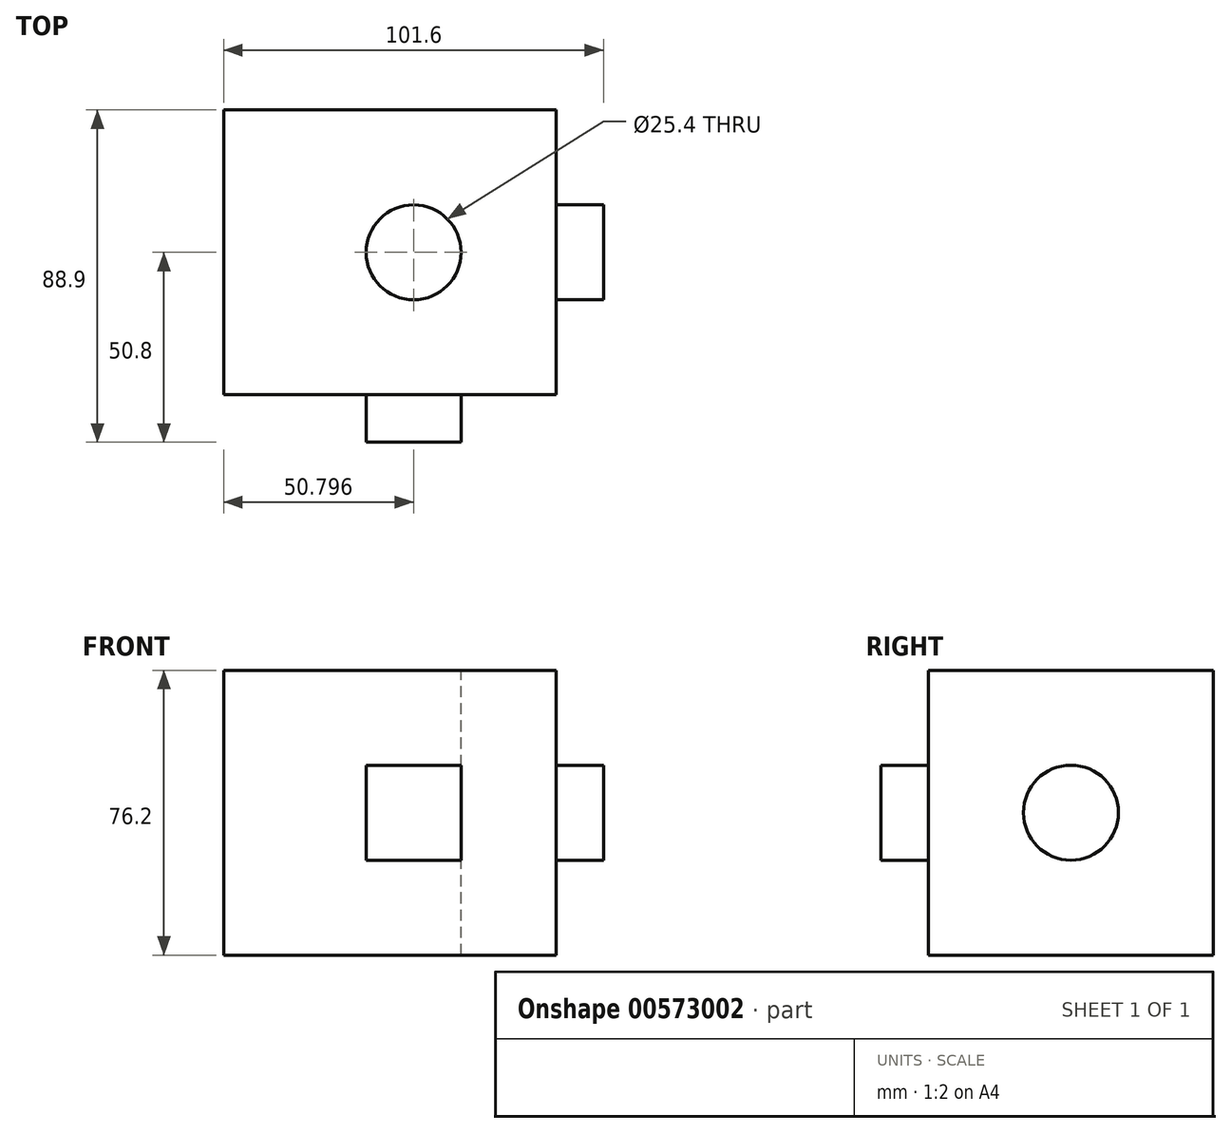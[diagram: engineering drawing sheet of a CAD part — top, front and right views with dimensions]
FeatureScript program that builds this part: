
annotation { "Feature Type Name" : "Feature", "Feature Type Description" : "" }
export const myFeature = defineFeature(function(context is Context, id is Id, definition is map)
    precondition{}
    {
        {
            var Q0;
            Q0=qCreatedBy(makeId("Front.planeOp"),FACE);
            var sketch = newSketch(context, id + "F0", { "sketchPlane" : qUnion([Q0])});
            skLineSegment(sketch, "E0.bottom", {"start": v(-75.57, 74.05) * mm, "end": v(0.63, 74.05) * mm});
            skLineSegment(sketch, "E0.top", {"start": v(-75.57, -2.15) * mm, "end": v(0.63, -2.15) * mm});
            skLineSegment(sketch, "E0.left", {"start": v(-75.57, 74.05) * mm, "end": v(-75.57, -2.15) * mm});
            skLineSegment(sketch, "E0.right", {"start": v(0.63, 74.05) * mm, "end": v(0.63, -2.15) * mm});
            skSolve(sketch);
        }
        {
            var Q0;
            Q0=makeQuery(id+"F0.imprint","IMPRINT",FACE,{"disambiguationData":[TD([[makeQuery(id+"F0.imprint","IMPRINT",EDGE,{"derivedFrom":sQuery(id+"F0.wireOp",EDGE,"E0.bottom")}),-1.0]])]});
            extrude(context, id + "F1", {"entities" : qUnion([Q0]), "depth" : 76.2 * mm, "offsetDistance" : 25.4 * mm});
        }
        {
            var Q0;
            Q0=makeQuery(id+"F1.opExtrude","SWEPT_FACE",FACE,{"disambiguationData":[OSD([sQuery(id+"F0.wireOp",EDGE,"E0.right")])]});
            var sketch = newSketch(context, id + "F2", { "sketchPlane" : qUnion([Q0])});
            skCircle(sketch, "E1", {"center": v(-38.1, 35.95) * mm, "radius": 12.7 * mm});
            skSolve(sketch);
        }
        {
            var Q0;
            Q0=makeQuery(id+"F2.imprint","IMPRINT",FACE,{"disambiguationData":[TD([[makeQuery(id+"F2.imprint","IMPRINT",EDGE,{"derivedFrom":sQuery(id+"F2.wireOp",EDGE,"E1")}),1.0]])]});
            extrude(context, id + "F3", {"entities" : qUnion([Q0]), "operationType" : NewBodyOperationType.ADD, "depth" : 12.7 * mm, "offsetDistance" : 25.4 * mm});
        }
        {
            var Q0;
            Q0=makeQuery(id+"F1.opExtrude","SWEPT_FACE",FACE,{"disambiguationData":[OSD([sQuery(id+"F0.wireOp",EDGE,"E0.bottom")])]});
            var sketch = newSketch(context, id + "F4", { "sketchPlane" : qUnion([Q0])});
            skPoint(sketch, "E2", {"position": v(-37.47, -38.1) * mm});
            skSolve(sketch);
        }
        {
            var Q0;
            Q0=sQuery(id+"F4.wireOp",VERTEX,"E2");
            var Q1;
            Q1=makeQuery(id+"F1.opExtrude","SWEPT_BODY",BODY,{"disambiguationData":[OSD([sQuery(id+"F0.wireOp",EDGE,"E0.bottom"),sQuery(id+"F0.wireOp",EDGE,"E0.top"),sQuery(id+"F0.wireOp",EDGE,"E0.left"),sQuery(id+"F0.wireOp",EDGE,"E0.right")])]});
            hole(context, id + "F5", {"style" : HoleStyle.SIMPLE, "endStyle" : HoleEndStyle.THROUGH, "holeDiameter" : 25.4 * mm, "isTappedThrough" : true, "tappedDepth" : 12.7 * mm, "tapClearance" : 3, "locations" : qUnion([Q0]), "scope" : qUnion([Q1])});
        }
        {
            var Q0;
            Q0=makeQuery(id+"F1.opExtrude","CAP_FACE",FACE,{"disambiguationData":[OSD([sQuery(id+"F0.wireOp",EDGE,"E0.bottom"),sQuery(id+"F0.wireOp",EDGE,"E0.top"),sQuery(id+"F0.wireOp",EDGE,"E0.left"),sQuery(id+"F0.wireOp",EDGE,"E0.right")])],"isStart":false});
            var sketch = newSketch(context, id + "F6", { "sketchPlane" : qUnion([Q0])});
            skLineSegment(sketch, "E3.bottom", {"start": v(-50.17, 48.65) * mm, "end": v(-24.77, 48.65) * mm});
            skLineSegment(sketch, "E3.top", {"start": v(-50.17, 23.25) * mm, "end": v(-24.77, 23.25) * mm});
            skLineSegment(sketch, "E3.left", {"start": v(-50.17, 48.65) * mm, "end": v(-50.17, 23.25) * mm});
            skLineSegment(sketch, "E3.right", {"start": v(-24.77, 48.65) * mm, "end": v(-24.77, 23.25) * mm});
            skSolve(sketch);
        }
        {
            var Q0;
            Q0 = qSketchRegion(id + "F6", true);
            extrude(context, id + "F7", {"entities" : qUnion([Q0]), "operationType" : NewBodyOperationType.ADD, "depth" : 12.7 * mm, "offsetDistance" : 25.4 * mm});
        }
        {
            var Q0;
            Q0=makeQuery(id+"F1.opExtrude","SWEPT_FACE",FACE,{"disambiguationData":[OSD([sQuery(id+"F0.wireOp",EDGE,"E0.left")])]});
            var sketch = newSketch(context, id + "F8", { "sketchPlane" : qUnion([Q0])});
            skCircle(sketch, "E4.cCircle", {"center": v(36.8, 39.1) * mm, "radius": 7.33 * mm, "construction": true});
            skLineSegment(sketch, "E4.0", {"start": v(48, 48.57) * mm, "end": v(39.42, 24.66) * mm});
            skLineSegment(sketch, "E4.1", {"start": v(39.42, 24.66) * mm, "end": v(23, 44.05) * mm});
            skLineSegment(sketch, "E4.2", {"start": v(23, 44.05) * mm, "end": v(48, 48.57) * mm});
            skPoint(sketch, "E4.0.midPoint", {"position": v(43.7, 36.62) * mm});
            skSolve(sketch);
        }
        {
            var Q0;
            Q0=makeQuery(id+"F8.imprint","IMPRINT",FACE,{"disambiguationData":[TD([[makeQuery(id+"F8.imprint","IMPRINT",EDGE,{"derivedFrom":sQuery(id+"F8.wireOp",EDGE,"E4.0")}),-1.0]])]});
            var Q1;
            Q1=makeQuery(id+"F8.imprint","IMPRINT",FACE,{"disambiguationData":[TD([[makeQuery(id+"F8.imprint","IMPRINT",EDGE,{"derivedFrom":sQuery(id+"F8.wireOp",EDGE,"E4.0")}),1.0]])]});
            extrude(context, id + "F9", {"entities" : qUnion([Q0, Q1]), "operationType" : NewBodyOperationType.ADD, "depth" : 12.7 * mm, "offsetDistance" : 25.4 * mm});
        }
    });
